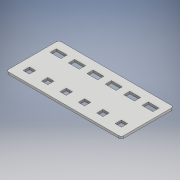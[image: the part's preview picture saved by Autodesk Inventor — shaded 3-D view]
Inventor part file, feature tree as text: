
AUTODESK INVENTOR PART (.ipt)
format: ipt  version: 2017 (Build 210142000, 142)  size: 169,984 bytes
history: native  units: mm
features: extrude x1, fillet x1, sketch x1
ambient origin geometry x8: Origin, YZ Plane, XZ Plane, XY Plane, X Axis, Y Axis, Z Axis, Center Point
bodies: Solid1 (feature_tree)
feature tree (3):
  extrude  "Extrusion1"  Depth=50.0mm
  fillet  "Fillet1"  Radius=5.0mm
  sketch  "Sketch1"  dims[d1=60.0mm d3=10.0mm d5=60.0mm d7=10.0mm d8=250.0mm d9=114.0mm d10=23.5mm d11=13.5mm d12=13.5mm d13=13.5mm d14=40.0mm d15=40.0mm d16=13.25mm d17=1.0mm d18=1.0mm d19=50.0mm d20=5.0mm d21=0.0mm d22=5.0mm]
